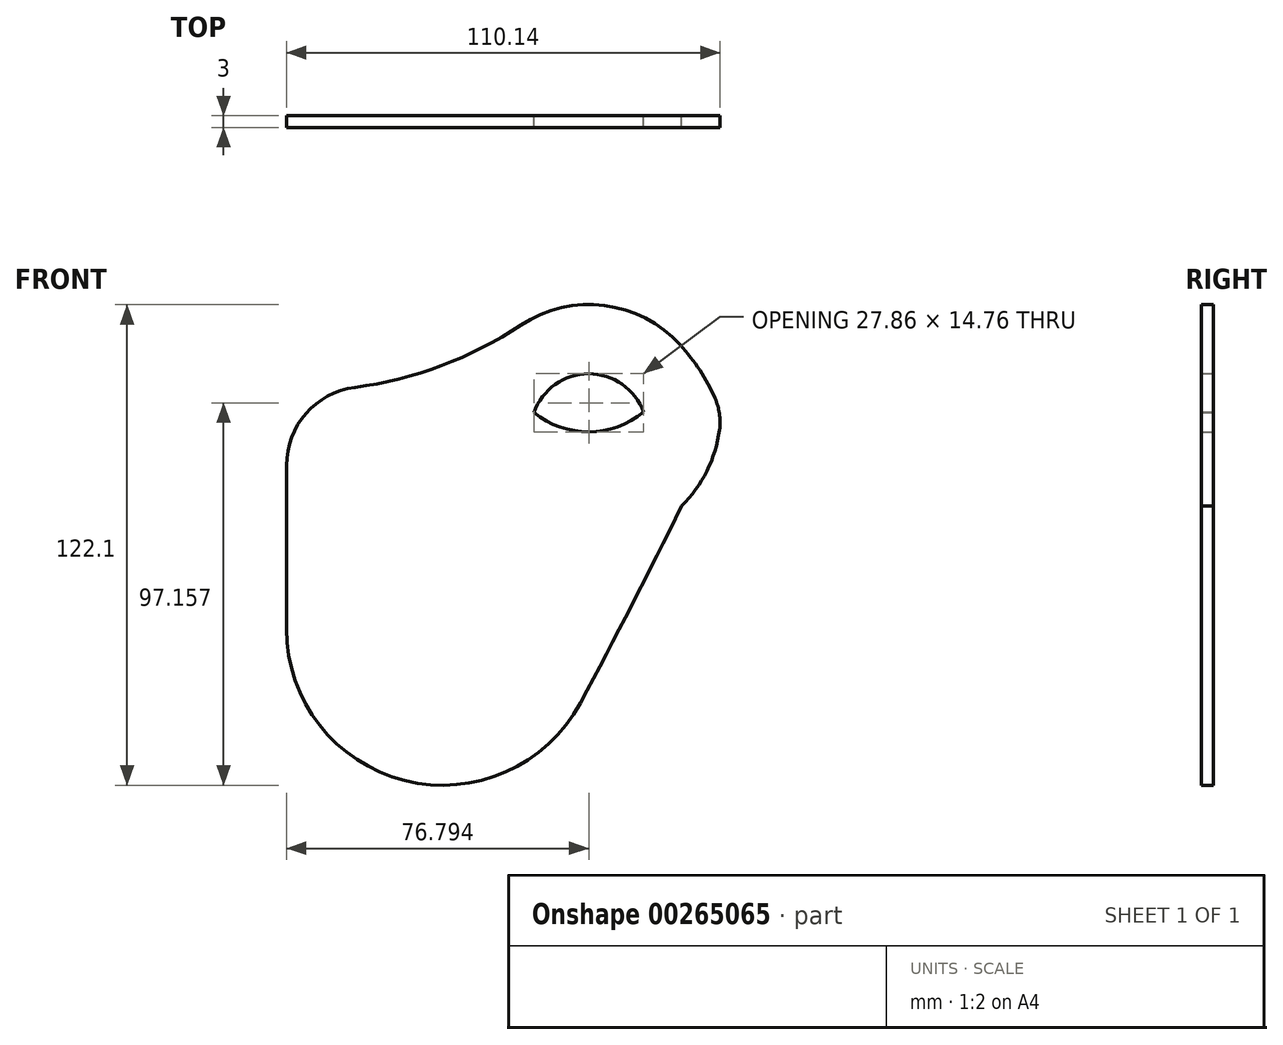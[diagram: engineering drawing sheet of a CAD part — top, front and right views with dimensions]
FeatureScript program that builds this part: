
annotation { "Feature Type Name" : "Feature", "Feature Type Description" : "" }
export const myFeature = defineFeature(function(context is Context, id is Id, definition is map)
    precondition{}
    {
        {
            var Q0;
            Q0=qCreatedBy(makeId("Front.planeOp"),FACE);
            var sketch = newSketch(context, id + "F0", { "sketchPlane" : qUnion([Q0])});
            skArc(sketch, "E0", {"start": v(-23.37, 71.6) * mm, "mid": v(-42.37, 87.06) * mm, "end": v(-61.37, 71.6) * mm});
            skPoint(sketch, "E1", {"position": v(-25.38, 77.03) * mm});
            skArc(sketch, "E2", {"start": v(-56.37, 71.6) * mm, "mid": v(-42.42, 66.69) * mm, "end": v(-28.5, 71.7) * mm});
            skArc(sketch, "E3", {"start": v(-28.5, 71.7) * mm, "mid": v(-42.48, 81.45) * mm, "end": v(-56.37, 71.6) * mm});
            skPoint(sketch, "E4", {"position": v(-42.37, 87.06) * mm});
            skPoint(sketch, "E5", {"position": v(-30.58, 56.7) * mm});
            skArc(sketch, "E6", {"start": v(-61.37, 71.6) * mm, "mid": v(-42.37, 52.6) * mm, "end": v(-23.37, 71.6) * mm});
            skPoint(sketch, "E7", {"position": v(-42.37, 52.6) * mm});
            skPoint(sketch, "E8", {"position": v(-61.37, 71.6) * mm});
            skPoint(sketch, "E9", {"position": v(-56.96, 80.44) * mm});
            skPoint(sketch, "E10", {"position": v(-68.92, 94.73) * mm});
            skArc(sketch, "E11", {"start": v(-57.31, 4.66) * mm, "mid": v(-44.8, 28.42) * mm, "end": v(-32.7, 52.4) * mm});
            skPoint(sketch, "E12", {"position": v(-29.37, 71.03) * mm});
            skLineSegment(sketch, "E13", {"start": v(-104.78, 66.2) * mm, "end": v(-104.78, 16.6) * mm});
            skArc(sketch, "E14", {"start": v(-104.78, 16.6) * mm, "mid": v(-85.7, -7.88) * mm, "end": v(-57.31, 4.66) * mm});
            skPoint(sketch, "E15", {"position": v(-85.15, 92.16) * mm});
            skPoint(sketch, "E16", {"position": v(-79.37, -8.64) * mm});
            skPoint(sketch, "E17.endSnap0", {"position": v(-42.4, 59.62) * mm});
            skLineSegment(sketch, "E18", {"start": v(-28.5, 71.7) * mm, "end": v(-23.37, 71.6) * mm});
            skLineSegment(sketch, "E19", {"start": v(-61.37, 71.6) * mm, "end": v(-56.37, 71.6) * mm});
            skLineSegment(sketch, "E20", {"start": v(-42.42, 66.69) * mm, "end": v(-42.42, 66.65) * mm});
            skPoint(sketch, "E21", {"position": v(-24.15, 66.23) * mm});
            skPoint(sketch, "E22", {"position": v(-59.84, 76.1) * mm});
            skPoint(sketch, "E23", {"position": v(-60.59, 66.2) * mm});
            skLineSegment(sketch, "E24.bottom", {"start": v(-26.7, 79.1) * mm, "end": v(-27.38, 79.1) * mm});
            skPoint(sketch, "E25", {"position": v(-108.66, 79.1) * mm});
            skLineSegment(sketch, "E26.top", {"start": v(-109.39, 67.1) * mm, "end": v(-109.78, 67.1) * mm});
            skLineSegment(sketch, "E27.left", {"start": v(-39.95, 71.09) * mm, "end": v(-39.95, 71.09) * mm});
            skLineSegment(sketch, "E27.right", {"start": v(-42.68, 71.09) * mm, "end": v(-42.68, 71.09) * mm});
            skLineSegment(sketch, "E28.top", {"start": v(-63.18, 66.2) * mm, "end": v(-68.59, 66.2) * mm});
            skPoint(sketch, "E29.orphan", {"position": v(-114.78, 67.1) * mm});
            skPoint(sketch, "E30.top.start.orphan", {"position": v(-109.78, 64.1) * mm});
            skPoint(sketch, "E17.end.orphan", {"position": v(-42.4, 81.45) * mm});
            skLineSegment(sketch, "E31.trimOffspring", {"start": v(-109.78, 54.6) * mm, "end": v(-109.78, 51.6) * mm});
            skPoint(sketch, "E32.top.end.orphan", {"position": v(-106.78, 10.37) * mm});
            skPoint(sketch, "E32.left.start.orphan", {"position": v(-109.78, 35.77) * mm});
            skPoint(sketch, "E27.bottom.start.orphan", {"position": v(-48.6, 10.37) * mm});
            skPoint(sketch, "E27.top.end.orphan", {"position": v(-51.33, 10.37) * mm});
            skPoint(sketch, "E33.start.orphan", {"position": v(-38.82, 35.77) * mm});
            skArc(sketch, "E34.0", {"start": v(-55.1, 3.47) * mm, "mid": v(-41.61, 29.17) * mm, "end": v(-28.58, 55.1) * mm});
            skArc(sketch, "E34.1", {"start": v(-107.28, 16.6) * mm, "mid": v(-86.31, -10.3) * mm, "end": v(-55.1, 3.47) * mm});
            skLineSegment(sketch, "E34.2", {"start": v(-107.28, 66.2) * mm, "end": v(-107.28, 16.6) * mm});
            skLineSegment(sketch, "E35", {"start": v(-20.87, 71.6) * mm, "end": v(-23.37, 71.6) * mm});
            skLineSegment(sketch, "E36", {"start": v(-68.59, 66.2) * mm, "end": v(-107.28, 66.2) * mm});
            skArc(sketch, "E37.0", {"start": v(-63.87, 71.6) * mm, "mid": v(-42.37, 50.1) * mm, "end": v(-20.87, 71.6) * mm});
            skLineSegment(sketch, "E38", {"start": v(-61.37, 71.6) * mm, "end": v(-63.87, 71.6) * mm});
            skPoint(sketch, "E39", {"position": v(-80.6, -11.12) * mm});
            skPoint(sketch, "E40", {"position": v(-80.6, 66.2) * mm});
            skArc(sketch, "E41.0", {"start": v(-44.59, -2.18) * mm, "mid": v(-31.5, 22.7) * mm, "end": v(-18.85, 47.82) * mm});
            skArc(sketch, "E41.1", {"start": v(-119.23, 16.6) * mm, "mid": v(-89.23, -21.89) * mm, "end": v(-44.59, -2.18) * mm});
            skLineSegment(sketch, "E41.2", {"start": v(-119.23, 66.2) * mm, "end": v(-119.23, 16.6) * mm});
            skArc(sketch, "E42.0", {"start": v(-11.67, 74.02) * mm, "mid": v(-40.22, 98.93) * mm, "end": v(-71.9, 78.15) * mm});
            skLineSegment(sketch, "E43.0", {"start": v(-71.9, 78.15) * mm, "end": v(-107.28, 78.15) * mm});
            skArc(sketch, "E44.0", {"start": v(-18.85, 47.82) * mm, "mid": v(-11.5, 58.71) * mm, "end": v(-8.93, 71.6) * mm});
            skLineSegment(sketch, "E45", {"start": v(-119.23, 66.2) * mm, "end": v(-119.23, 78.15) * mm});
            skLineSegment(sketch, "E46", {"start": v(-107.28, 78.15) * mm, "end": v(-119.23, 78.15) * mm});
            skLineSegment(sketch, "E47", {"start": v(-8.93, 71.6) * mm, "end": v(-11.67, 71.6) * mm});
            skLineSegment(sketch, "E48", {"start": v(-11.67, 71.6) * mm, "end": v(-11.67, 74.02) * mm});
            skPoint(sketch, "E49.orphan", {"position": v(-73.06, 74.02) * mm});
            skPoint(sketch, "E50.end.orphan", {"position": v(-73.06, 71.6) * mm});
            skPoint(sketch, "E51.orphan", {"position": v(-119.23, 79.1) * mm});
            skPoint(sketch, "E52", {"position": v(-19.16, 88.73) * mm});
            skArc(sketch, "E53", {"start": v(-8.93, 71.6) * mm, "mid": v(-13.18, 80.68) * mm, "end": v(-19.16, 88.73) * mm});
            skSolve(sketch);
        }
        {
            var Q0;
            Q0=makeQuery(id+"F0.imprint","IMPRINT",FACE,{"disambiguationData":[TD([[makeQuery(id+"F0.imprint","IMPRINT",EDGE,{"derivedFrom":sQuery(id+"F0.wireOp",EDGE,"E3")}),-1.0]])]});
            var Q1;
            {var subQ2=sQuery(id+"F0.wireOp",EDGE,"E11");Q1=makeQuery(id+"F0.imprint","IMPRINT",FACE,{"disambiguationData":[TD([[makeQuery(id+"F0.imprint","IMPRINT",EDGE,{"derivedFrom":subQ2}),-1.0]])]});}
            var Q2;
            Q2=makeQuery(id+"F0.imprint","IMPRINT",FACE,{"disambiguationData":[TD([[makeQuery(id+"F0.imprint","IMPRINT",EDGE,{"derivedFrom":sQuery(id+"F0.wireOp",EDGE,"E6")}),1.0]])]});
            var Q3;
            {var subQ1=sQuery(id+"F0.wireOp",EDGE,"E11");Q3=makeQuery(id+"F0.imprint","IMPRINT",FACE,{"disambiguationData":[TD([[makeQuery(id+"F0.imprint","IMPRINT",EDGE,{"derivedFrom":subQ1}),1.0]])]});}
            var Q4;
            {var subQ0=sQuery(id+"F0.wireOp",EDGE,"E3");Q4=makeQuery(id+"F0.imprint","IMPRINT",FACE,{"disambiguationData":[TD([[makeQuery(id+"F0.imprint","IMPRINT",EDGE,{"derivedFrom":subQ0}),1.0]])]});}
            var Q5;
            Q5=makeQuery(id+"F0.imprint","IMPRINT",FACE,{"disambiguationData":[TD([[makeQuery(id+"F0.imprint","IMPRINT",EDGE,{"derivedFrom":sQuery(id+"F0.wireOp",EDGE,"E6")}),-1.0]])]});
            var Q6;
            {var subQ1=sQuery(id+"F0.wireOp",EDGE,"E28.top");Q6=makeQuery(id+"F0.imprint","IMPRINT",FACE,{"disambiguationData":[TD([[makeQuery(id+"F0.imprint","IMPRINT",EDGE,{"derivedFrom":subQ1}),-1.0]])]});}
            var Q7;
            Q7=makeQuery(id+"F0.imprint","IMPRINT",FACE,{"disambiguationData":[TD([[makeQuery(id+"F0.imprint","IMPRINT",EDGE,{"derivedFrom":sQuery(id+"F0.wireOp",EDGE,"E47")}),-1.0]])]});
            extrude(context, id + "F1", {"entities" : qUnion([Q0, Q1, Q2, Q3, Q4, Q5, Q6, Q7]), "depth" : 3 * mm, "offsetDistance" : 25 * mm});
        }
        {
            var Q0;
            {var subQ0=sQuery(id+"F0.wireOp",EDGE,"E3");Q0=makeQuery(id+"F0.imprint","IMPRINT",FACE,{"disambiguationData":[TD([[makeQuery(id+"F0.imprint","IMPRINT",EDGE,{"derivedFrom":subQ0}),1.0]])]});}
            extrude(context, id + "F2", {"entities" : qUnion([Q0]), "operationType" : NewBodyOperationType.REMOVE, "depth" : 25 * mm, "offsetDistance" : 25 * mm});
        }
        {
            var Q0;
            Q0=makeQuery(id+"F1.opExtrude","SWEPT_EDGE",EDGE,{"disambiguationData":[OSD([sQuery(id+"F0.wireOp",EDGE,"E45"),sQuery(id+"F0.wireOp",EDGE,"E46")])]});
            fillet(context, id + "F3", {"entities" : qUnion([Q0]), "radius" : 20 * mm, "tangentPropagation" : true, "allowEdgeOverflow" : false});
        }
        {
            var Q0;
            Q0=makeQuery(id+"F1.opExtrude","SWEPT_EDGE",EDGE,{"disambiguationData":[OSD([sQuery(id+"F0.wireOp",EDGE,"E42.0"),sQuery(id+"F0.wireOp",EDGE,"E43.0")])]});
            fillet(context, id + "F4", {"entities" : qUnion([Q0]), "radius" : 100 * mm, "tangentPropagation" : true, "defaultsChanged" : false, "vertexSettings" : [], "allowEdgeOverflow" : false});
        }
        {
            var Q0;
            Q0=makeQuery(id+"F1.opExtrude","SWEPT_EDGE",EDGE,{"disambiguationData":[OSD([sQuery(id+"F0.wireOp",EDGE,"E44.0"),sQuery(id+"F0.wireOp",EDGE,"E47")])]});
            fillet(context, id + "F5", {"entities" : qUnion([Q0]), "radius" : 15 * mm, "tangentPropagation" : true, "allowEdgeOverflow" : false});
        }
    });
